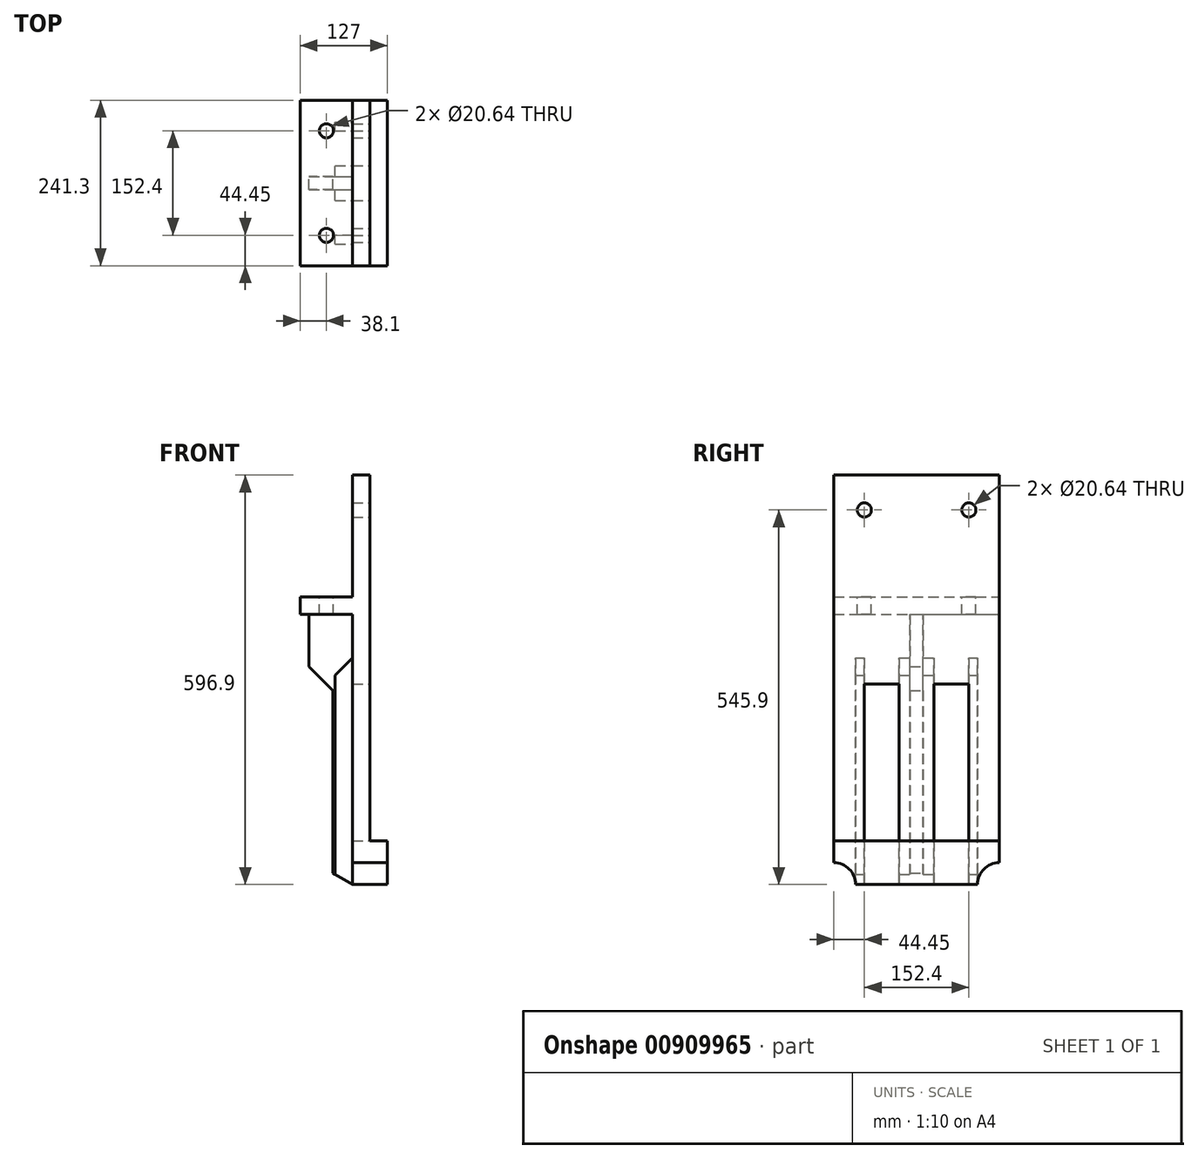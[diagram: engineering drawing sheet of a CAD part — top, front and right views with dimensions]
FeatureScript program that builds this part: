
annotation { "Feature Type Name" : "Feature", "Feature Type Description" : "" }
export const myFeature = defineFeature(function(context is Context, id is Id, definition is map)
    precondition{}
    {
        {
            var Q0;
            Q0=qCreatedBy(makeId("Front.planeOp"),FACE);
            var sketch = newSketch(context, id + "F0", { "sketchPlane" : qUnion([Q0])});
            skLineSegment(sketch, "E0", {"start": v(0, 0) * mm, "end": v(0, 533.6) * mm});
            skLineSegment(sketch, "E1", {"start": v(0, 533.6) * mm, "end": v(-25.4, 533.6) * mm});
            skLineSegment(sketch, "E2", {"start": v(-25.4, 533.6) * mm, "end": v(-25.4, 355.73) * mm});
            skLineSegment(sketch, "E3", {"start": v(-25.4, 355.73) * mm, "end": v(-101.6, 355.73) * mm});
            skLineSegment(sketch, "E4", {"start": v(-101.6, 355.73) * mm, "end": v(-101.6, 330.33) * mm});
            skLineSegment(sketch, "E5", {"start": v(-101.6, 330.33) * mm, "end": v(-25.4, 330.33) * mm});
            skLineSegment(sketch, "E6", {"start": v(-25.4, 330.33) * mm, "end": v(-25.4, -63.3) * mm});
            skLineSegment(sketch, "E7", {"start": v(-25.4, -63.3) * mm, "end": v(25.4, -63.3) * mm});
            skLineSegment(sketch, "E8", {"start": v(25.4, -63.3) * mm, "end": v(25.4, 0) * mm});
            skLineSegment(sketch, "E9", {"start": v(25.4, 0) * mm, "end": v(0, 0) * mm});
            skLineSegment(sketch, "E10", {"start": v(-25.4, 228.6) * mm, "end": v(0, 228.6) * mm});
            skLineSegment(sketch, "E11", {"start": v(-25.4, 0) * mm, "end": v(0, 0) * mm});
            skSolve(sketch);
        }
        {
            var Q0;
            Q0=makeQuery(id+"F0.imprint","IMPRINT",FACE,{"disambiguationData":[TD([[makeQuery(id+"F0.imprint","IMPRINT",EDGE,{"derivedFrom":sQuery(id+"F0.wireOp",EDGE,"E0")}),1.0]])]});
            var Q1;
            {var subQ0=sQuery(id+"F0.wireOp",EDGE,"E1");Q1=makeQuery(id+"F0.imprint","IMPRINT",FACE,{"disambiguationData":[TD([[makeQuery(id+"F0.imprint","IMPRINT",EDGE,{"derivedFrom":subQ0}),1.0]])]});}
            var Q2;
            {var subQ0=sQuery(id+"F0.wireOp",EDGE,"E7");Q2=makeQuery(id+"F0.imprint","IMPRINT",FACE,{"disambiguationData":[TD([[makeQuery(id+"F0.imprint","IMPRINT",EDGE,{"derivedFrom":subQ0}),1.0]])]});}
            extrude(context, id + "F1", {"entities" : qUnion([Q0, Q1, Q2]), "depth" : 241.3 * mm, "offsetDistance" : 25 * mm, "symmetric" : true});
        }
        {
            var Q0;
            {var subQ0=sQuery(id+"F0.wireOp",EDGE,"E10");Q0=makeQuery(id+"F0.imprint","IMPRINT",FACE,{"disambiguationData":[TD([[makeQuery(id+"F0.imprint","IMPRINT",EDGE,{"derivedFrom":subQ0}),-1.0]])]});}
            extrude(context, id + "F2", {"entities" : qUnion([Q0]), "operationType" : NewBodyOperationType.REMOVE, "oppositeDirection" : true, "depth" : 152.4 * mm, "offsetDistance" : 25 * mm, "symmetric" : true});
        }
        {
            var Q0;
            {var subQ0=sQuery(id+"F0.wireOp",EDGE,"E10");Q0=makeQuery(id+"F0.imprint","IMPRINT",FACE,{"disambiguationData":[TD([[makeQuery(id+"F0.imprint","IMPRINT",EDGE,{"derivedFrom":subQ0}),-1.0]])]});}
            extrude(context, id + "F3", {"entities" : qUnion([Q0]), "operationType" : NewBodyOperationType.ADD, "depth" : 50.8 * mm, "offsetDistance" : 25 * mm, "symmetric" : true});
        }
        {
            var Q0;
            {var subQ0=sQuery(id+"F0.wireOp",EDGE,"E0");Q0=makeQuery(id+"F3.boolean.opBoolean","MERGE",FACE,{"derivedFrom":[makeQuery(id+"F1.opExtrude","SWEPT_FACE",FACE,{"disambiguationData":[OSD([subQ0])]}),makeQuery(id+"F3.opExtrude","SWEPT_FACE",FACE,{"disambiguationData":[OSD([subQ0])]})]});}
            var sketch = newSketch(context, id + "F4", { "sketchPlane" : qUnion([Q0])});
            skLineSegment(sketch, "E12", {"start": v(-76.2, 482.6) * mm, "end": v(76.2, 482.6) * mm, "construction": true});
            skLineSegment(sketch, "E13", {"start": v(0, 482.6) * mm, "end": v(0, 0) * mm, "construction": true});
            skCircle(sketch, "E14", {"center": v(-76.2, 482.6) * mm, "radius": 10.32 * mm});
            skCircle(sketch, "E15", {"center": v(76.2, 482.6) * mm, "radius": 10.32 * mm});
            skSolve(sketch);
        }
        {
            var Q0;
            Q0=makeQuery(id+"F4.imprint","IMPRINT",FACE,{"disambiguationData":[TD([[makeQuery(id+"F4.imprint","IMPRINT",EDGE,{"derivedFrom":sQuery(id+"F4.wireOp",EDGE,"E14")}),1.0]])]});
            var Q1;
            Q1=makeQuery(id+"F4.imprint","IMPRINT",FACE,{"disambiguationData":[TD([[makeQuery(id+"F4.imprint","IMPRINT",EDGE,{"derivedFrom":sQuery(id+"F4.wireOp",EDGE,"E15")}),1.0]])]});
            extrude(context, id + "F5", {"entities" : qUnion([Q0, Q1]), "operationType" : NewBodyOperationType.REMOVE, "endBound" : BoundingType.THROUGH_ALL, "oppositeDirection" : true, "depth" : 25 * mm, "offsetDistance" : 25 * mm});
        }
        {
            var Q0;
            Q0=makeQuery(id+"F1.opExtrude","SWEPT_FACE",FACE,{"disambiguationData":[OSD([sQuery(id+"F0.wireOp",EDGE,"E8")])]});
            var sketch = newSketch(context, id + "F6", { "sketchPlane" : qUnion([Q0])});
            skCircle(sketch, "E16", {"center": v(-120.65, -63.3) * mm, "radius": 31.75 * mm});
            skCircle(sketch, "E17", {"center": v(120.65, -63.3) * mm, "radius": 31.75 * mm});
            skSolve(sketch);
        }
        {
            var Q0;
            {var subQ0=sQuery(id+"F6.wireOp",EDGE,"E16");var subQ1=sQuery(id+"F0.wireOp",EDGE,"E8");var subQ4=makeQuery(id+"F1.opExtrude","CAP_EDGE",EDGE,{"disambiguationData":[OSD([subQ1])],"isStart":false});var subQ5=makeQuery(id+"F6.imprint","INTERSECT",VERTEX,{"derivedFrom":[subQ4,subQ0]});Q0=makeQuery(id+"F6.imprint","IMPRINT",FACE,{"disambiguationData":[TD([[makeQuery(id+"F6.imprint","IMPRINT",EDGE,{"disambiguationData":[TD([[subQ5,1.0]])],"derivedFrom":subQ0}),1.0]])]});}
            var Q1;
            {var subQ0=sQuery(id+"F6.wireOp",EDGE,"E17");var subQ1=sQuery(id+"F0.wireOp",EDGE,"E8");var subQ4=makeQuery(id+"F1.opExtrude","CAP_EDGE",EDGE,{"disambiguationData":[OSD([subQ1])],"isStart":true});var subQ5=makeQuery(id+"F6.imprint","INTERSECT",VERTEX,{"derivedFrom":[subQ4,subQ0]});Q1=makeQuery(id+"F6.imprint","IMPRINT",FACE,{"disambiguationData":[TD([[makeQuery(id+"F6.imprint","IMPRINT",EDGE,{"disambiguationData":[TD([[subQ5,-1.0]])],"derivedFrom":subQ0}),1.0]])]});}
            extrude(context, id + "F7", {"entities" : qUnion([Q0, Q1]), "operationType" : NewBodyOperationType.REMOVE, "endBound" : BoundingType.THROUGH_ALL, "oppositeDirection" : true, "depth" : 25 * mm, "offsetDistance" : 25 * mm});
        }
        {
            var Q0;
            Q0=qCreatedBy(makeId("Front.planeOp"),FACE);
            var sketch = newSketch(context, id + "F8", { "sketchPlane" : qUnion([Q0])});
            skLineSegment(sketch, "E18", {"start": v(-25.4, -63.3) * mm, "end": v(-50.8, -48.64) * mm});
            skLineSegment(sketch, "E19", {"start": v(-50.8, -48.64) * mm, "end": v(-50.8, 216.03) * mm});
            skLineSegment(sketch, "E20", {"start": v(-50.8, 216.03) * mm, "end": v(-88.9, 254.13) * mm});
            skLineSegment(sketch, "E21", {"start": v(-88.9, 254.13) * mm, "end": v(-88.9, 330.33) * mm});
            skLineSegment(sketch, "E22", {"start": v(-88.9, 330.33) * mm, "end": v(-25.4, 330.33) * mm});
            skLineSegment(sketch, "E23", {"start": v(-25.4, 330.33) * mm, "end": v(-25.4, -63.3) * mm});
            skLineSegment(sketch, "E24", {"start": v(-50.8, 216.03) * mm, "end": v(-50.8, 241.43) * mm});
            skLineSegment(sketch, "E25", {"start": v(-50.8, 241.43) * mm, "end": v(-25.4, 266.83) * mm});
            skLineSegment(sketch, "E26", {"start": v(-53.98, 219.2) * mm, "end": v(-53.97, -46.8) * mm});
            skLineSegment(sketch, "E27", {"start": v(-53.97, -46.8) * mm, "end": v(-50.8, -48.64) * mm});
            skSolve(sketch);
        }
        {
            var Q0;
            {var subQ1=sQuery(id+"F8.wireOp",EDGE,"E18");Q0=makeQuery(id+"F8.imprint","IMPRINT",FACE,{"disambiguationData":[TD([[makeQuery(id+"F8.imprint","IMPRINT",EDGE,{"derivedFrom":subQ1}),-1.0]])]});}
            extrude(context, id + "F9", {"entities" : qUnion([Q0]), "operationType" : NewBodyOperationType.ADD, "depth" : 177.8 * mm, "offsetDistance" : 25 * mm, "symmetric" : true});
        }
        {
            var Q0;
            {var subQ1=sQuery(id+"F8.wireOp",EDGE,"E18");Q0=makeQuery(id+"F8.imprint","IMPRINT",FACE,{"disambiguationData":[TD([[makeQuery(id+"F8.imprint","IMPRINT",EDGE,{"derivedFrom":subQ1}),-1.0]])]});}
            extrude(context, id + "F10", {"entities" : qUnion([Q0]), "operationType" : NewBodyOperationType.REMOVE, "oppositeDirection" : true, "depth" : 152.4 * mm, "offsetDistance" : 25 * mm, "symmetric" : true});
        }
        {
            var Q0;
            {var subQ1=sQuery(id+"F8.wireOp",EDGE,"E18");Q0=makeQuery(id+"F8.imprint","IMPRINT",FACE,{"disambiguationData":[TD([[makeQuery(id+"F8.imprint","IMPRINT",EDGE,{"derivedFrom":subQ1}),-1.0]])]});}
            extrude(context, id + "F11", {"entities" : qUnion([Q0]), "operationType" : NewBodyOperationType.ADD, "depth" : 50.8 * mm, "offsetDistance" : 25 * mm, "symmetric" : true});
        }
        {
            var Q0;
            Q0=makeQuery(id+"F8.imprint","IMPRINT",FACE,{"disambiguationData":[TD([[makeQuery(id+"F8.imprint","IMPRINT",EDGE,{"derivedFrom":sQuery(id+"F8.wireOp",EDGE,"E20")}),-1.0]])]});
            var Q1;
            {var subQ0=sQuery(id+"F8.wireOp",EDGE,"E19");Q1=makeQuery(id+"F8.imprint","IMPRINT",FACE,{"disambiguationData":[TD([[makeQuery(id+"F8.imprint","IMPRINT",EDGE,{"derivedFrom":subQ0}),1.0]])]});}
            extrude(context, id + "F12", {"entities" : qUnion([Q0, Q1]), "operationType" : NewBodyOperationType.ADD, "depth" : 19.05 * mm, "offsetDistance" : 25 * mm, "symmetric" : true});
        }
        {
            var Q0;
            Q0=makeQuery(id+"F1.opExtrude","SWEPT_FACE",FACE,{"disambiguationData":[OSD([sQuery(id+"F0.wireOp",EDGE,"E3")])]});
            var sketch = newSketch(context, id + "F13", { "sketchPlane" : qUnion([Q0])});
            skLineSegment(sketch, "E28", {"start": v(-63.5, 76.2) * mm, "end": v(-63.5, -76.2) * mm, "construction": true});
            skLineSegment(sketch, "E29", {"start": v(-63.5, 0) * mm, "end": v(0, 0) * mm, "construction": true});
            skCircle(sketch, "E30", {"center": v(-63.5, 76.2) * mm, "radius": 10.32 * mm});
            skCircle(sketch, "E31", {"center": v(-63.5, -76.2) * mm, "radius": 10.32 * mm});
            skSolve(sketch);
        }
        {
            var Q0;
            Q0=makeQuery(id+"F13.imprint","IMPRINT",FACE,{"disambiguationData":[TD([[makeQuery(id+"F13.imprint","IMPRINT",EDGE,{"derivedFrom":sQuery(id+"F13.wireOp",EDGE,"E30")}),1.0]])]});
            var Q1;
            Q1=makeQuery(id+"F13.imprint","IMPRINT",FACE,{"disambiguationData":[TD([[makeQuery(id+"F13.imprint","IMPRINT",EDGE,{"derivedFrom":sQuery(id+"F13.wireOp",EDGE,"E31")}),1.0]])]});
            extrude(context, id + "F14", {"entities" : qUnion([Q0, Q1]), "operationType" : NewBodyOperationType.REMOVE, "endBound" : BoundingType.THROUGH_ALL, "oppositeDirection" : true, "depth" : 25 * mm, "offsetDistance" : 25 * mm});
        }
    });
